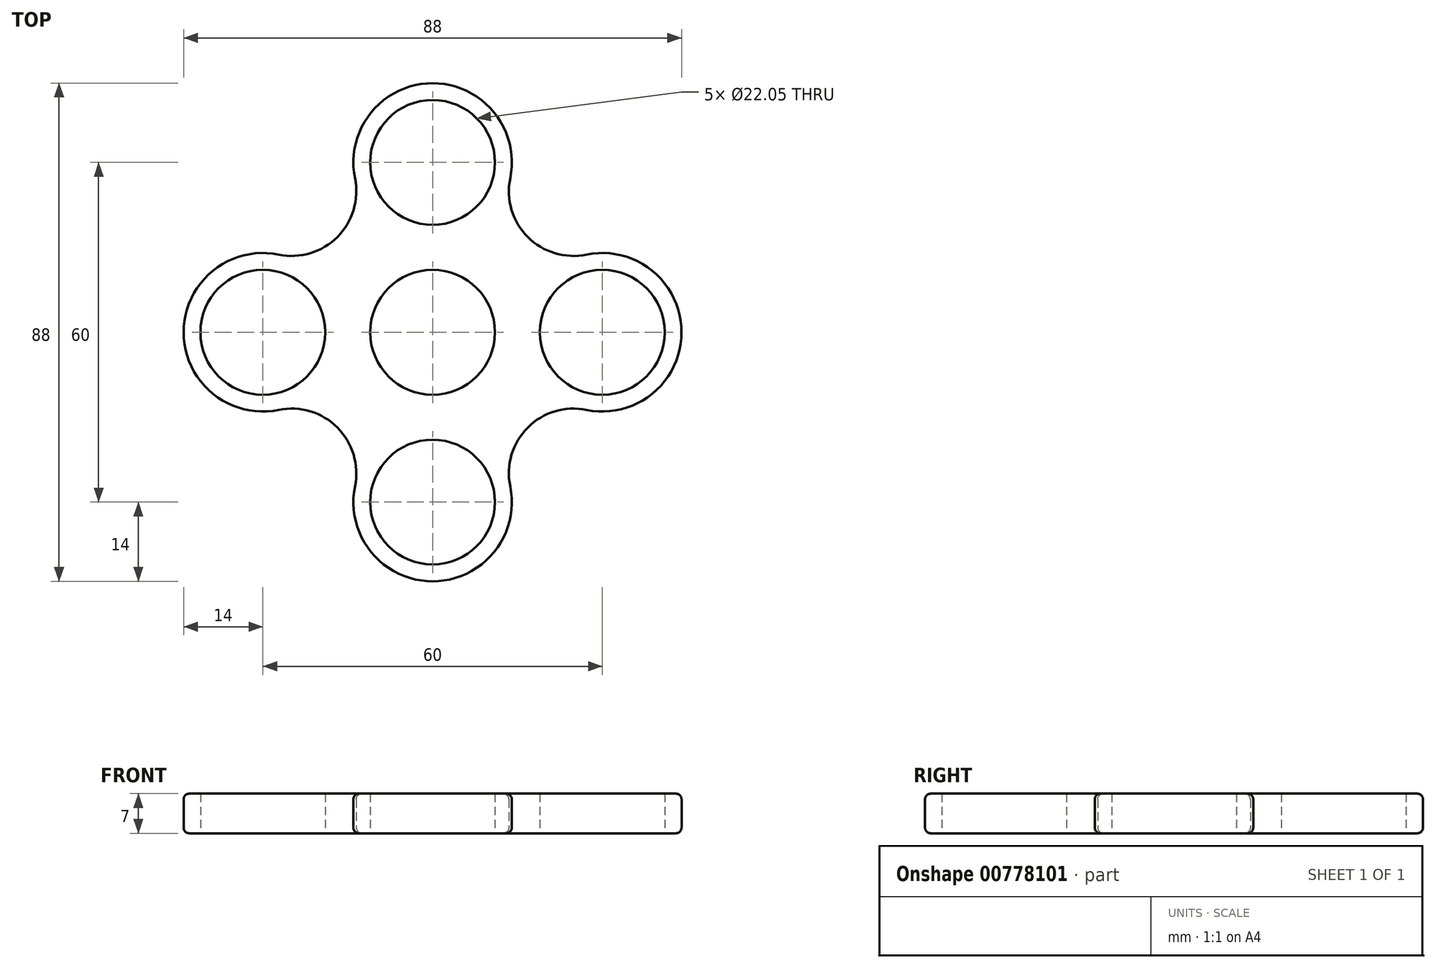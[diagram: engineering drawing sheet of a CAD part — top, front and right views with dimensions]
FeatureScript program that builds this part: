
annotation { "Feature Type Name" : "Feature", "Feature Type Description" : "" }
export const myFeature = defineFeature(function(context is Context, id is Id, definition is map)
    precondition{}
    {
        {
            var Q0;
            Q0=qCreatedBy(makeId("Top.planeOp"),FACE);
            var sketch = newSketch(context, id + "F0", { "sketchPlane" : qUnion([Q0])});
            skLineSegment(sketch, "E0.bottom", {"start": v(30, 30) * mm, "end": v(-30, 30) * mm, "construction": true});
            skLineSegment(sketch, "E0.top", {"start": v(30, -30) * mm, "end": v(-30, -30) * mm, "construction": true});
            skLineSegment(sketch, "E0.left", {"start": v(30, 30) * mm, "end": v(30, -30) * mm, "construction": true});
            skLineSegment(sketch, "E0.right", {"start": v(-30, 30) * mm, "end": v(-30, -30) * mm, "construction": true});
            skPoint(sketch, "E0.middle", {"position": v(0, 0) * mm});
            skCircle(sketch, "E1", {"center": v(0, 30) * mm, "radius": 14 * mm});
            skCircle(sketch, "E2", {"center": v(30, 0) * mm, "radius": 14 * mm});
            skCircle(sketch, "E3", {"center": v(0, -30) * mm, "radius": 14 * mm});
            skCircle(sketch, "E4", {"center": v(-30, 0) * mm, "radius": 14 * mm});
            skCircle(sketch, "E5", {"center": v(0, 0) * mm, "radius": 14 * mm});
            skCircle(sketch, "E6", {"center": v(0, 30) * mm, "radius": 11.03 * mm});
            skCircle(sketch, "E7", {"center": v(30, 0) * mm, "radius": 11.03 * mm});
            skCircle(sketch, "E8", {"center": v(0, -30) * mm, "radius": 11.03 * mm});
            skCircle(sketch, "E9", {"center": v(0, 0) * mm, "radius": 11.03 * mm});
            skCircle(sketch, "E10", {"center": v(-30, 0) * mm, "radius": 11.03 * mm});
            skArc(sketch, "E11", {"start": v(13.72, 27.2) * mm, "mid": v(16.83, 16.83) * mm, "end": v(27.2, 13.72) * mm});
            skLineSegment(sketch, "E12", {"start": v(9.9, 39.9) * mm, "end": v(39.9, 9.9) * mm, "construction": true});
            skArc(sketch, "E13.MirrorCS", {"start": v(-13.72, 27.2) * mm, "mid": v(-16.83, 16.83) * mm, "end": v(-27.2, 13.72) * mm});
            skArc(sketch, "E14.MirrorCS", {"start": v(13.72, -27.2) * mm, "mid": v(16.83, -16.83) * mm, "end": v(27.2, -13.72) * mm});
            skArc(sketch, "E15.MirrorCS", {"start": v(-13.72, -27.2) * mm, "mid": v(-16.83, -16.83) * mm, "end": v(-27.2, -13.72) * mm});
            skSolve(sketch);
        }
        {
            var Q0;
            Q0=makeQuery(id+"F0.imprint","IMPRINT",FACE,{"disambiguationData":[TD([[makeQuery(id+"F0.imprint","IMPRINT",EDGE,{"derivedFrom":sQuery(id+"F0.wireOp",EDGE,"E5")}),-1.0]])]});
            var Q1;
            Q1=makeQuery(id+"F0.imprint","IMPRINT",FACE,{"disambiguationData":[TD([[makeQuery(id+"F0.imprint","IMPRINT",EDGE,{"derivedFrom":sQuery(id+"F0.wireOp",EDGE,"E5")}),1.0]])]});
            var Q2;
            Q2=makeQuery(id+"F0.imprint","IMPRINT",FACE,{"disambiguationData":[TD([[makeQuery(id+"F0.imprint","IMPRINT",EDGE,{"derivedFrom":sQuery(id+"F0.wireOp",EDGE,"E7")}),-1.0]])]});
            var Q3;
            Q3=makeQuery(id+"F0.imprint","IMPRINT",FACE,{"disambiguationData":[TD([[makeQuery(id+"F0.imprint","IMPRINT",EDGE,{"derivedFrom":sQuery(id+"F0.wireOp",EDGE,"E8")}),-1.0]])]});
            var Q4;
            Q4=makeQuery(id+"F0.imprint","IMPRINT",FACE,{"disambiguationData":[TD([[makeQuery(id+"F0.imprint","IMPRINT",EDGE,{"derivedFrom":sQuery(id+"F0.wireOp",EDGE,"E10")}),-1.0]])]});
            var Q5;
            Q5=makeQuery(id+"F0.imprint","IMPRINT",FACE,{"disambiguationData":[TD([[makeQuery(id+"F0.imprint","IMPRINT",EDGE,{"derivedFrom":sQuery(id+"F0.wireOp",EDGE,"E6")}),-1.0]])]});
            extrude(context, id + "F1", {"entities" : qUnion([Q0, Q1, Q2, Q3, Q4, Q5]), "depth" : 7 * mm, "offsetDistance" : 25 * mm});
        }
        {
            var Q0;
            Q0=makeQuery(id+"F1.opExtrude","SWEPT_FACE",FACE,{"disambiguationData":[OSD([sQuery(id+"F0.wireOp",EDGE,"E3")])]});
            var Q1;
            Q1=makeQuery(id+"F1.opExtrude","SWEPT_FACE",FACE,{"disambiguationData":[OSD([sQuery(id+"F0.wireOp",EDGE,"E14.MirrorCS")])]});
            var Q2;
            Q2=makeQuery(id+"F1.opExtrude","SWEPT_FACE",FACE,{"disambiguationData":[OSD([sQuery(id+"F0.wireOp",EDGE,"E2")])]});
            var Q3;
            Q3=makeQuery(id+"F1.opExtrude","SWEPT_FACE",FACE,{"disambiguationData":[OSD([sQuery(id+"F0.wireOp",EDGE,"E4")])]});
            var Q4;
            Q4=makeQuery(id+"F1.opExtrude","SWEPT_FACE",FACE,{"disambiguationData":[OSD([sQuery(id+"F0.wireOp",EDGE,"E15.MirrorCS")])]});
            var Q5;
            Q5=makeQuery(id+"F1.opExtrude","SWEPT_FACE",FACE,{"disambiguationData":[OSD([sQuery(id+"F0.wireOp",EDGE,"E1")])]});
            var Q6;
            Q6=makeQuery(id+"F1.opExtrude","SWEPT_FACE",FACE,{"disambiguationData":[OSD([sQuery(id+"F0.wireOp",EDGE,"E11")])]});
            var Q7;
            Q7=makeQuery(id+"F1.opExtrude","SWEPT_FACE",FACE,{"disambiguationData":[OSD([sQuery(id+"F0.wireOp",EDGE,"E13.MirrorCS")])]});
            fillet(context, id + "F2", {"entities" : qUnion([Q0, Q1, Q2, Q3, Q4, Q5, Q6, Q7]), "radius" : 1 * mm, "tangentPropagation" : true, "allowEdgeOverflow" : false});
        }
    });
